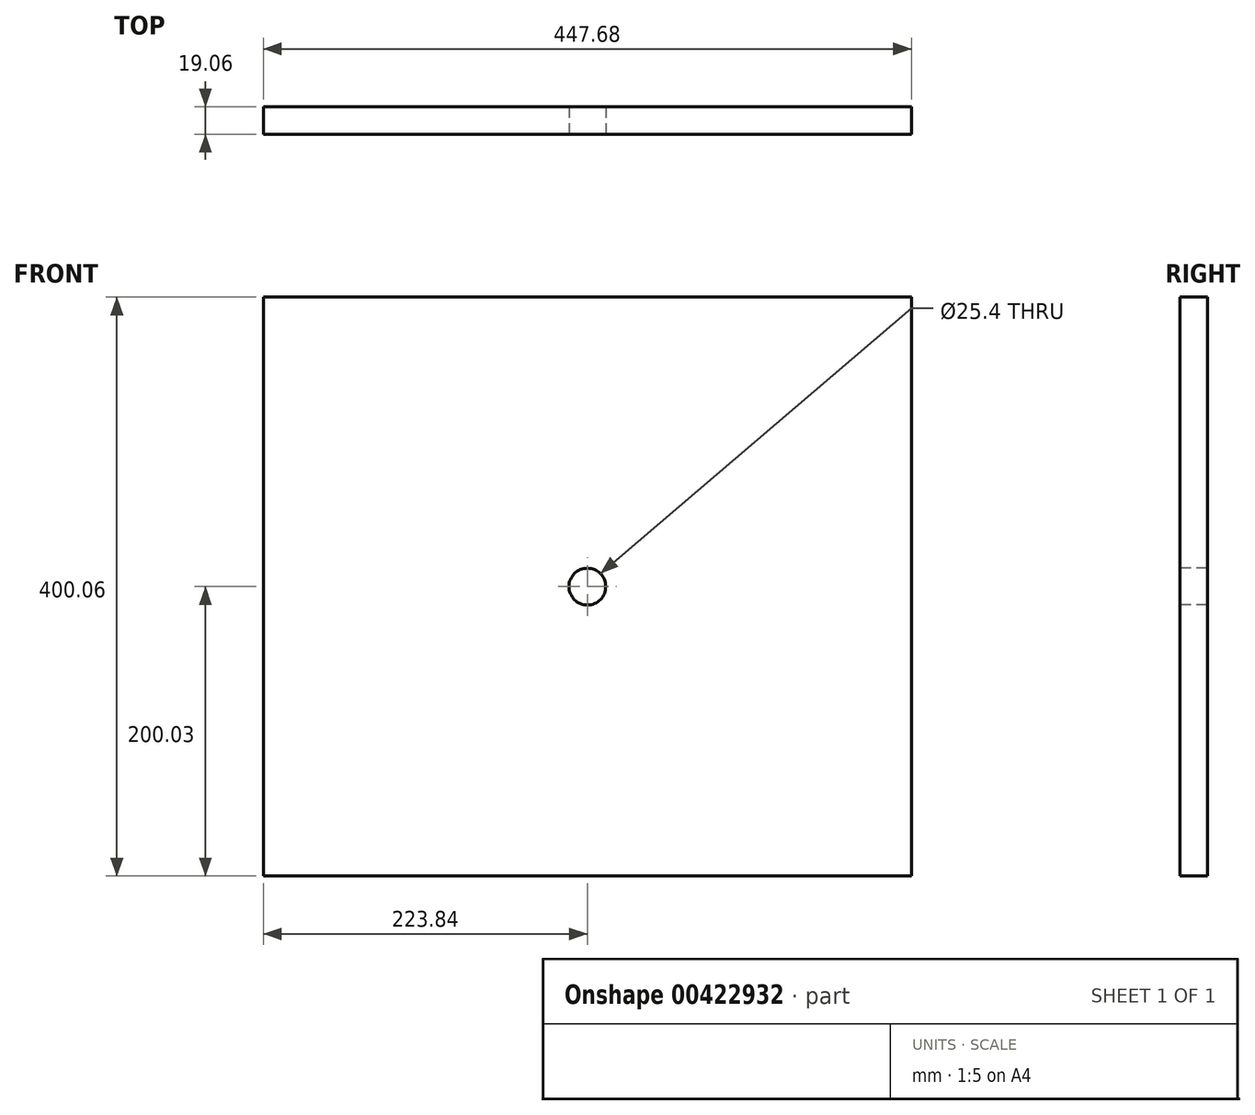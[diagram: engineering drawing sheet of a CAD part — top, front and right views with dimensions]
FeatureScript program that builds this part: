
annotation { "Feature Type Name" : "Feature", "Feature Type Description" : "" }
export const myFeature = defineFeature(function(context is Context, id is Id, definition is map)
    precondition{}
    {
        {
            var Q0;
            Q0=qCreatedBy(makeId("Front.planeOp"),FACE);
            var sketch = newSketch(context, id + "F0", { "sketchPlane" : qUnion([Q0])});
            skLineSegment(sketch, "E0.bottom", {"start": v(223.84, 200.03) * mm, "end": v(-223.84, 200.03) * mm});
            skLineSegment(sketch, "E0.top", {"start": v(223.84, -200.03) * mm, "end": v(-223.84, -200.03) * mm});
            skLineSegment(sketch, "E0.left", {"start": v(223.84, 200.03) * mm, "end": v(223.84, -200.03) * mm});
            skLineSegment(sketch, "E0.right", {"start": v(-223.84, 200.03) * mm, "end": v(-223.84, -200.03) * mm});
            skPoint(sketch, "E0.middle", {"position": v(0, 0) * mm});
            skSolve(sketch);
        }
        {
            var Q0;
            Q0=makeQuery(id+"F0.imprint","IMPRINT",FACE,{"disambiguationData":[TD([[makeQuery(id+"F0.imprint","IMPRINT",EDGE,{"derivedFrom":sQuery(id+"F0.wireOp",EDGE,"E0.bottom")}),1.0]])]});
            extrude(context, id + "F1", {"entities" : qUnion([Q0]), "endBound" : BoundingType.SYMMETRIC, "depth" : 19.05 * mm});
        }
        {
            var Q0;
            Q0=makeQuery(id+"F1.opExtrude","CAP_FACE",FACE,{"disambiguationData":[OSD([sQuery(id+"F0.wireOp",EDGE,"E0.bottom"),sQuery(id+"F0.wireOp",EDGE,"E0.top"),sQuery(id+"F0.wireOp",EDGE,"E0.left"),sQuery(id+"F0.wireOp",EDGE,"E0.right")])],"isStart":false});
            var sketch = newSketch(context, id + "F2", { "sketchPlane" : qUnion([Q0])});
            skCircle(sketch, "E1", {"center": v(0, 0) * mm, "radius": 12.7 * mm});
            skSolve(sketch);
        }
        {
            var Q0;
            Q0=qSketchRegion(id+"F2",true);
            extrude(context, id + "F3", {"entities" : qUnion([Q0]), "operationType" : NewBodyOperationType.REMOVE, "oppositeDirection" : true, "depth" : 25.4 * mm});
        }
    });
